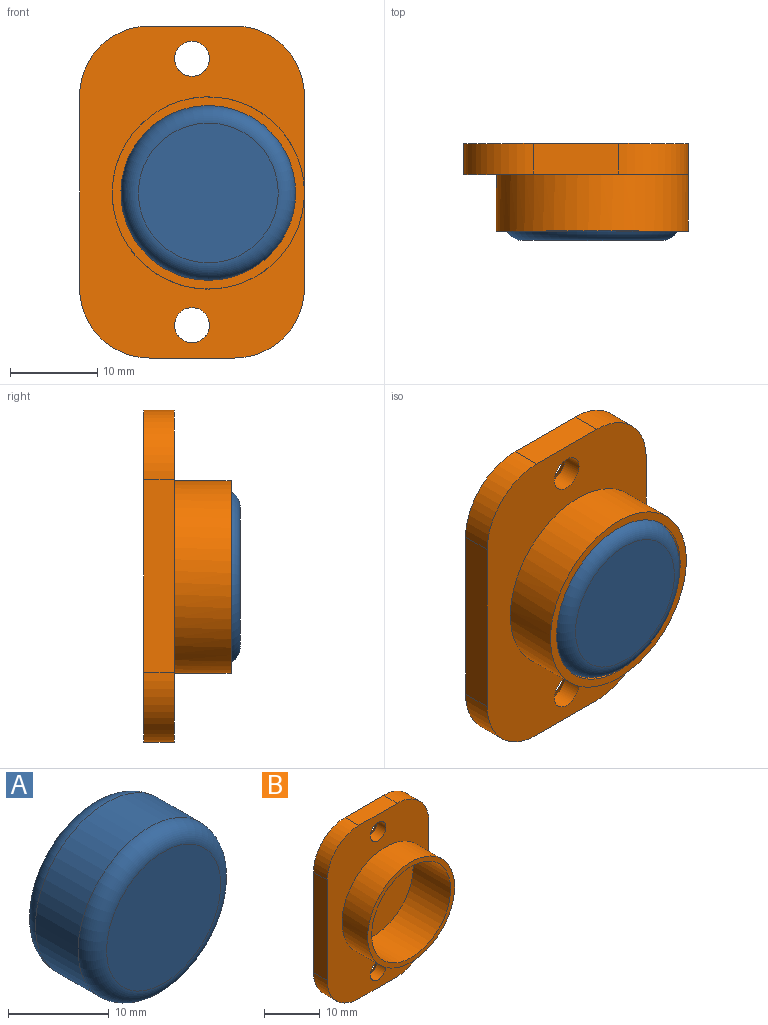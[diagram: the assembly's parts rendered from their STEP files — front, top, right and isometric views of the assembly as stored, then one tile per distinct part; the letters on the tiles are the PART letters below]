
ASSEMBLY  parts=2 mates=1
PART A: 5 faces, bbox 21.6x10x21.6 mm
  f0: cylinder r=10mm len=20mm, axis (0,1,0), area 377mm2, adj f3,f4
  f1: plane 16x16mm, normal (0,-1,0), area 201.1mm2, adj f4
  f2: plane 16x16mm, normal (0,1,0), area 201.1mm2, adj f3
  f3: torus R=8mm, axis (0,-1,0), area 183mm2, adj f0,f2
  f4: torus R=8mm, axis (0,-1,0), area 183mm2, adj f0,f1
PART B: 18 faces, bbox 25.7x10x38 mm
  f0: plane 22x3.5mm, normal (1,0,0), area 77mm2, adj f4,f5,f14,f17
  f1: plane 9.73x3.5mm, normal (0,0,1), area 34.1mm2, adj f4,f5,f14,f15
  f2: plane 22x3.5mm, normal (-1,0,0), area 77mm2, adj f4,f5,f15,f16
  f3: plane 9.73x3.5mm, normal (0,0,-1), area 34.1mm2, adj f4,f5,f16,f17
  f4: plane 38x25.73mm, normal (0,-1,0), area 517.7mm2, adj f0,f1,f2,f3,f7,f10,f12,f14
  f5: plane 38x25.73mm, normal (0,1,0), area 856.6mm2, adj f0,f1,f2,f3,f11,f13,f14,f15
  f6: cylinder r=10mm len=20mm, axis (0,1,0), area 596.9mm2, adj f8,f9
  f7: cylinder r=11mm len=22mm, axis (0,1,0), area 449.2mm2, adj f4,f8
  f8: plane 22x22mm, normal (0,-1,0), area 66mm2, adj f6,f7
  f9: plane 20x20mm, normal (0,-1,0), area 314.2mm2, adj f6
  f10: cylinder r=2mm len=4mm, axis (0,1,0), area 28.3mm2, adj f4,f11
  f11: cone r=2mm half-angle=45deg, axis (0,1,0), area 29.2mm2, adj f5,f10
  f12: cylinder r=2mm len=4mm, axis (0,1,0), area 28.3mm2, adj f4,f13
  f13: cone r=2mm half-angle=45deg, axis (0,1,0), area 29.2mm2, adj f5,f12
  f14: cylinder r=8mm len=8mm, axis (0,-1,0), area 44mm2, adj f0,f1,f4,f5
  f15: cylinder r=8mm len=8mm, axis (0,1,0), area 44mm2, adj f1,f2,f4,f5
  f16: cylinder r=8mm len=8mm, axis (0,-1,0), area 44mm2, adj f2,f3,f4,f5
  f17: cylinder r=8mm len=8mm, axis (0,1,0), area 44mm2, adj f0,f3,f4,f5
PLACE A t=(45.81,-35.74,11.48)mm
PLACE B t=(41.81,-34.69,11.48)mm fixed
MATE slider B.f6 <-> A.f0  axis (0,-1,0) through (45.81,-35.19,11.48)mm
